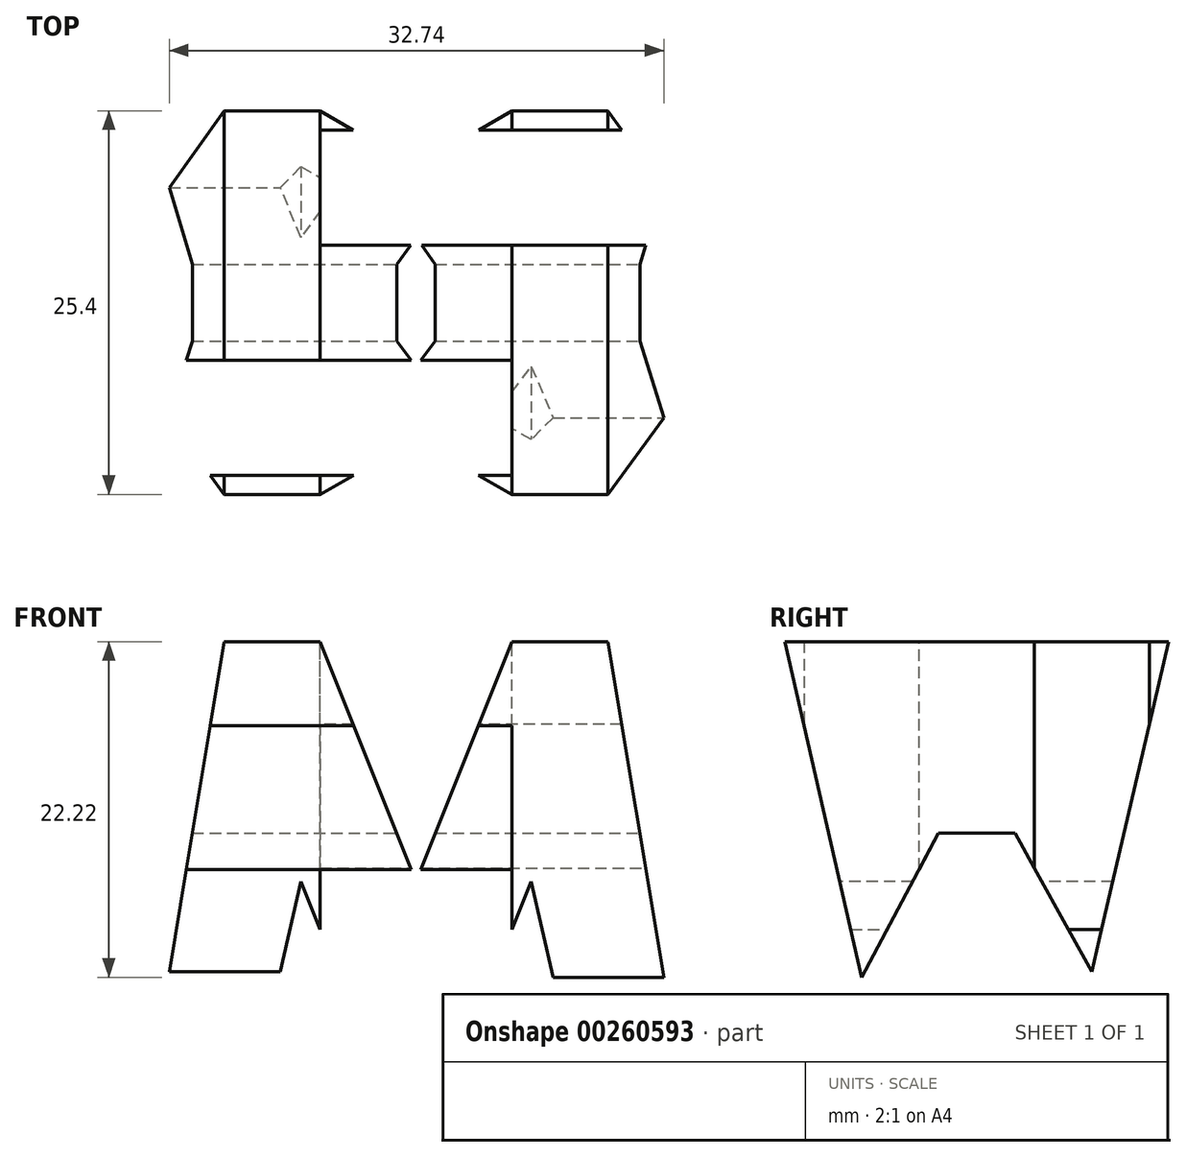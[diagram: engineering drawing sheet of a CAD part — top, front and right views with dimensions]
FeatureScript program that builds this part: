
annotation { "Feature Type Name" : "Feature", "Feature Type Description" : "" }
export const myFeature = defineFeature(function(context is Context, id is Id, definition is map)
    precondition{}
    {
        {
            var Q0;
            Q0=qCreatedBy(makeId("Front.planeOp"),FACE);
            var sketch = newSketch(context, id + "F0", { "sketchPlane" : qUnion([Q0])});
            skLineSegment(sketch, "E0", {"start": v(0, 0) * mm, "end": v(0, 38.1) * mm});
            skLineSegment(sketch, "E1", {"start": v(0, 38.1) * mm, "end": v(38.1, 38.1) * mm});
            skLineSegment(sketch, "E2", {"start": v(38.1, 38.1) * mm, "end": v(38.1, 0) * mm});
            skLineSegment(sketch, "E3", {"start": v(38.1, 0) * mm, "end": v(0, 0) * mm});
            skSolve(sketch);
        }
        {
            var Q0;
            Q0=makeQuery(id+"F0.imprint","IMPRINT",FACE,{"disambiguationData":[TD([[makeQuery(id+"F0.imprint","IMPRINT",EDGE,{"derivedFrom":sQuery(id+"F0.wireOp",EDGE,"E0")}),-1.0]])]});
            extrude(context, id + "F1", {"entities" : qUnion([Q0]), "depth" : 38.1 * mm});
        }
        {
            var Q0;
            Q0=qCreatedBy(makeId("Front.planeOp"),FACE);
            cPlane(context, id + "F2", {"entities" : qUnion([Q0]), "cplaneType" : CPlaneType.OFFSET, "offset" : 38.1 * mm, "width" : 152.4 * mm, "height" : 152.4 * mm});
        }
        {
            var Q0;
            Q0=qCreatedBy(makeId("Right.planeOp"),FACE);
            cPlane(context, id + "F3", {"entities" : qUnion([Q0]), "cplaneType" : CPlaneType.OFFSET, "offset" : 38.1 * mm, "width" : 152.4 * mm, "height" : 152.4 * mm});
        }
        {
            var Q0;
            Q0=qCreatedBy(makeId("Top.planeOp"),FACE);
            cPlane(context, id + "F4", {"entities" : qUnion([Q0]), "cplaneType" : CPlaneType.OFFSET, "offset" : 38.1 * mm, "width" : 152.4 * mm, "height" : 152.4 * mm});
        }
        {
            var Q0;
            Q0=qCreatedBy(id+"F3.planeOp",FACE);
            var sketch = newSketch(context, id + "F5", { "sketchPlane" : qUnion([Q0])});
            skLineSegment(sketch, "E4", {"start": v(0, 0) * mm, "end": v(0, 38.1) * mm});
            skLineSegment(sketch, "E5", {"start": v(0, 38.1) * mm, "end": v(-38.1, 38.1) * mm});
            skLineSegment(sketch, "E6", {"start": v(-38.1, 38.1) * mm, "end": v(-38.1, 0) * mm});
            skLineSegment(sketch, "E7", {"start": v(-38.1, 0) * mm, "end": v(0, 0) * mm});
            skLineSegment(sketch, "E8", {"start": v(-38.1, 38.1) * mm, "end": v(-31.75, 0) * mm});
            skLineSegment(sketch, "E9", {"start": v(-31.75, 0) * mm, "end": v(-25.4, 0) * mm});
            skLineSegment(sketch, "E10", {"start": v(-25.4, 0) * mm, "end": v(-19.05, 12.71) * mm});
            skPoint(sketch, "E10.endSnap0", {"position": v(-19.05, -3.16) * mm});
            skLineSegment(sketch, "E11", {"start": v(-19.05, 12.71) * mm, "end": v(-12.7, 0) * mm});
            skLineSegment(sketch, "E12", {"start": v(-12.7, 0) * mm, "end": v(-6.35, 0) * mm});
            skLineSegment(sketch, "E13", {"start": v(-6.35, 0) * mm, "end": v(0, 38.1) * mm});
            skLineSegment(sketch, "E14", {"start": v(0, 38.1) * mm, "end": v(-6.35, 38.1) * mm});
            skLineSegment(sketch, "E15", {"start": v(-6.35, 38.1) * mm, "end": v(-11.43, 16.25) * mm});
            skLineSegment(sketch, "E16", {"start": v(-11.43, 16.25) * mm, "end": v(-16.51, 25.41) * mm});
            skLineSegment(sketch, "E17", {"start": v(-16.51, 25.41) * mm, "end": v(-21.6, 25.41) * mm});
            skLineSegment(sketch, "E18", {"start": v(-21.59, 25.41) * mm, "end": v(-26.67, 15.87) * mm});
            skLineSegment(sketch, "E19", {"start": v(-26.67, 15.88) * mm, "end": v(-31.75, 38.1) * mm});
            skLineSegment(sketch, "E20", {"start": v(-38.1, 38.1) * mm, "end": v(-31.75, 38.1) * mm});
            skLineSegment(sketch, "E21", {"start": v(-6.35, 38.1) * mm, "end": v(0, 38.1) * mm});
            skSolve(sketch);
        }
        {
            var Q0;
            Q0=makeQuery(id+"F5.imprint","IMPRINT",FACE,{"disambiguationData":[TD([[makeQuery(id+"F5.imprint","IMPRINT",EDGE,{"derivedFrom":sQuery(id+"F5.wireOp",EDGE,"E5")}),1.0]])]});
            var Q1;
            {var subQ0=sQuery(id+"F5.wireOp",EDGE,"E6");Q1=makeQuery(id+"F5.imprint","IMPRINT",FACE,{"disambiguationData":[TD([[makeQuery(id+"F5.imprint","IMPRINT",EDGE,{"derivedFrom":subQ0}),1.0]])]});}
            var Q2;
            {var subQ0=sQuery(id+"F5.wireOp",EDGE,"E10");Q2=makeQuery(id+"F5.imprint","IMPRINT",FACE,{"disambiguationData":[TD([[makeQuery(id+"F5.imprint","IMPRINT",EDGE,{"derivedFrom":subQ0}),-1.0]])]});}
            var Q3;
            {var subQ0=sQuery(id+"F5.wireOp",EDGE,"E4");Q3=makeQuery(id+"F5.imprint","IMPRINT",FACE,{"disambiguationData":[TD([[makeQuery(id+"F5.imprint","IMPRINT",EDGE,{"derivedFrom":subQ0}),1.0]])]});}
            extrude(context, id + "F6", {"entities" : qUnion([Q0, Q1, Q2, Q3]), "operationType" : NewBodyOperationType.REMOVE, "oppositeDirection" : true, "depth" : 38.1 * mm});
        }
        {
            var Q0;
            Q0=qCreatedBy(id+"F2.planeOp",FACE);
            var sketch = newSketch(context, id + "F7", { "sketchPlane" : qUnion([Q0])});
            skLineSegment(sketch, "E22", {"start": v(0, 0) * mm, "end": v(0, 38.1) * mm});
            skLineSegment(sketch, "E23", {"start": v(0, 38.1) * mm, "end": v(38.1, 38.1) * mm});
            skLineSegment(sketch, "E24", {"start": v(38.1, 38.1) * mm, "end": v(38.1, 0) * mm});
            skLineSegment(sketch, "E25", {"start": v(38.1, 0) * mm, "end": v(0, 0) * mm});
            skLineSegment(sketch, "E26", {"start": v(6.35, 38.1) * mm, "end": v(0, 0) * mm});
            skLineSegment(sketch, "E27", {"start": v(6.35, 0) * mm, "end": v(11.43, 22.23) * mm});
            skLineSegment(sketch, "E28", {"start": v(11.43, 22.23) * mm, "end": v(16.51, 9.52) * mm});
            skLineSegment(sketch, "E29", {"start": v(16.51, 9.52) * mm, "end": v(21.6, 9.52) * mm});
            skLineSegment(sketch, "E30", {"start": v(21.6, 9.52) * mm, "end": v(26.67, 22.23) * mm});
            skLineSegment(sketch, "E31", {"start": v(26.67, 22.23) * mm, "end": v(31.75, 0) * mm});
            skLineSegment(sketch, "E32", {"start": v(31.75, 0) * mm, "end": v(38.1, 0) * mm});
            skLineSegment(sketch, "E33", {"start": v(38.1, 0) * mm, "end": v(31.75, 38.1) * mm});
            skLineSegment(sketch, "E34", {"start": v(25.4, 38.1) * mm, "end": v(19.05, 22.22) * mm});
            skLineSegment(sketch, "E35", {"start": v(12.7, 38.1) * mm, "end": v(19.05, 22.22) * mm});
            skLineSegment(sketch, "E36", {"start": v(12.7, 38.1) * mm, "end": v(6.35, 38.1) * mm});
            skSolve(sketch);
        }
        {
            var Q0;
            {var subQ0=sQuery(id+"F7.wireOp",EDGE,"E22");Q0=makeQuery(id+"F7.imprint","IMPRINT",FACE,{"disambiguationData":[TD([[makeQuery(id+"F7.imprint","IMPRINT",EDGE,{"derivedFrom":subQ0}),-1.0]])]});}
            var Q1;
            {var subQ0=sQuery(id+"F7.wireOp",EDGE,"E34");Q1=makeQuery(id+"F7.imprint","IMPRINT",FACE,{"disambiguationData":[TD([[makeQuery(id+"F7.imprint","IMPRINT",EDGE,{"derivedFrom":subQ0}),-1.0]])]});}
            var Q2;
            {var subQ0=sQuery(id+"F7.wireOp",EDGE,"E27");Q2=makeQuery(id+"F7.imprint","IMPRINT",FACE,{"disambiguationData":[TD([[makeQuery(id+"F7.imprint","IMPRINT",EDGE,{"derivedFrom":subQ0}),-1.0]])]});}
            var Q3;
            {var subQ0=sQuery(id+"F7.wireOp",EDGE,"E24");Q3=makeQuery(id+"F7.imprint","IMPRINT",FACE,{"disambiguationData":[TD([[makeQuery(id+"F7.imprint","IMPRINT",EDGE,{"derivedFrom":subQ0}),-1.0]])]});}
            extrude(context, id + "F8", {"entities" : qUnion([Q0, Q1, Q2, Q3]), "operationType" : NewBodyOperationType.REMOVE, "oppositeDirection" : true, "depth" : 38.1 * mm});
        }
        {
            var Q0;
            Q0=qCreatedBy(id+"F4.planeOp",FACE);
            var sketch = newSketch(context, id + "F9", { "sketchPlane" : qUnion([Q0])});
            skLineSegment(sketch, "E37", {"start": v(0, -38.1) * mm, "end": v(0, 0) * mm});
            skLineSegment(sketch, "E38", {"start": v(0, 0) * mm, "end": v(38.1, 0) * mm});
            skLineSegment(sketch, "E39", {"start": v(38.1, 0) * mm, "end": v(38.1, -38.1) * mm});
            skLineSegment(sketch, "E40", {"start": v(38.1, -38.1) * mm, "end": v(0, -38.1) * mm});
            skLineSegment(sketch, "E41", {"start": v(38.1, -7.62) * mm, "end": v(12.7, -7.62) * mm});
            skLineSegment(sketch, "E42", {"start": v(12.7, -7.62) * mm, "end": v(12.7, -15.24) * mm});
            skLineSegment(sketch, "E43", {"start": v(12.7, -15.24) * mm, "end": v(38.1, -15.24) * mm});
            skLineSegment(sketch, "E44", {"start": v(0, -22.86) * mm, "end": v(25.4, -22.86) * mm});
            skLineSegment(sketch, "E45", {"start": v(25.4, -22.86) * mm, "end": v(25.4, -30.48) * mm});
            skLineSegment(sketch, "E46", {"start": v(25.4, -30.48) * mm, "end": v(0, -30.48) * mm});
            skSolve(sketch);
        }
        {
            var Q0;
            {var subQ0=sQuery(id+"F9.wireOp",EDGE,"E41");Q0=makeQuery(id+"F9.imprint","IMPRINT",FACE,{"disambiguationData":[TD([[makeQuery(id+"F9.imprint","IMPRINT",EDGE,{"derivedFrom":subQ0}),1.0]])]});}
            var Q1;
            {var subQ0=sQuery(id+"F9.wireOp",EDGE,"E44");Q1=makeQuery(id+"F9.imprint","IMPRINT",FACE,{"disambiguationData":[TD([[makeQuery(id+"F9.imprint","IMPRINT",EDGE,{"derivedFrom":subQ0}),-1.0]])]});}
            extrude(context, id + "F10", {"entities" : qUnion([Q0, Q1]), "operationType" : NewBodyOperationType.REMOVE, "oppositeDirection" : true, "depth" : 38.1 * mm});
        }
    });
